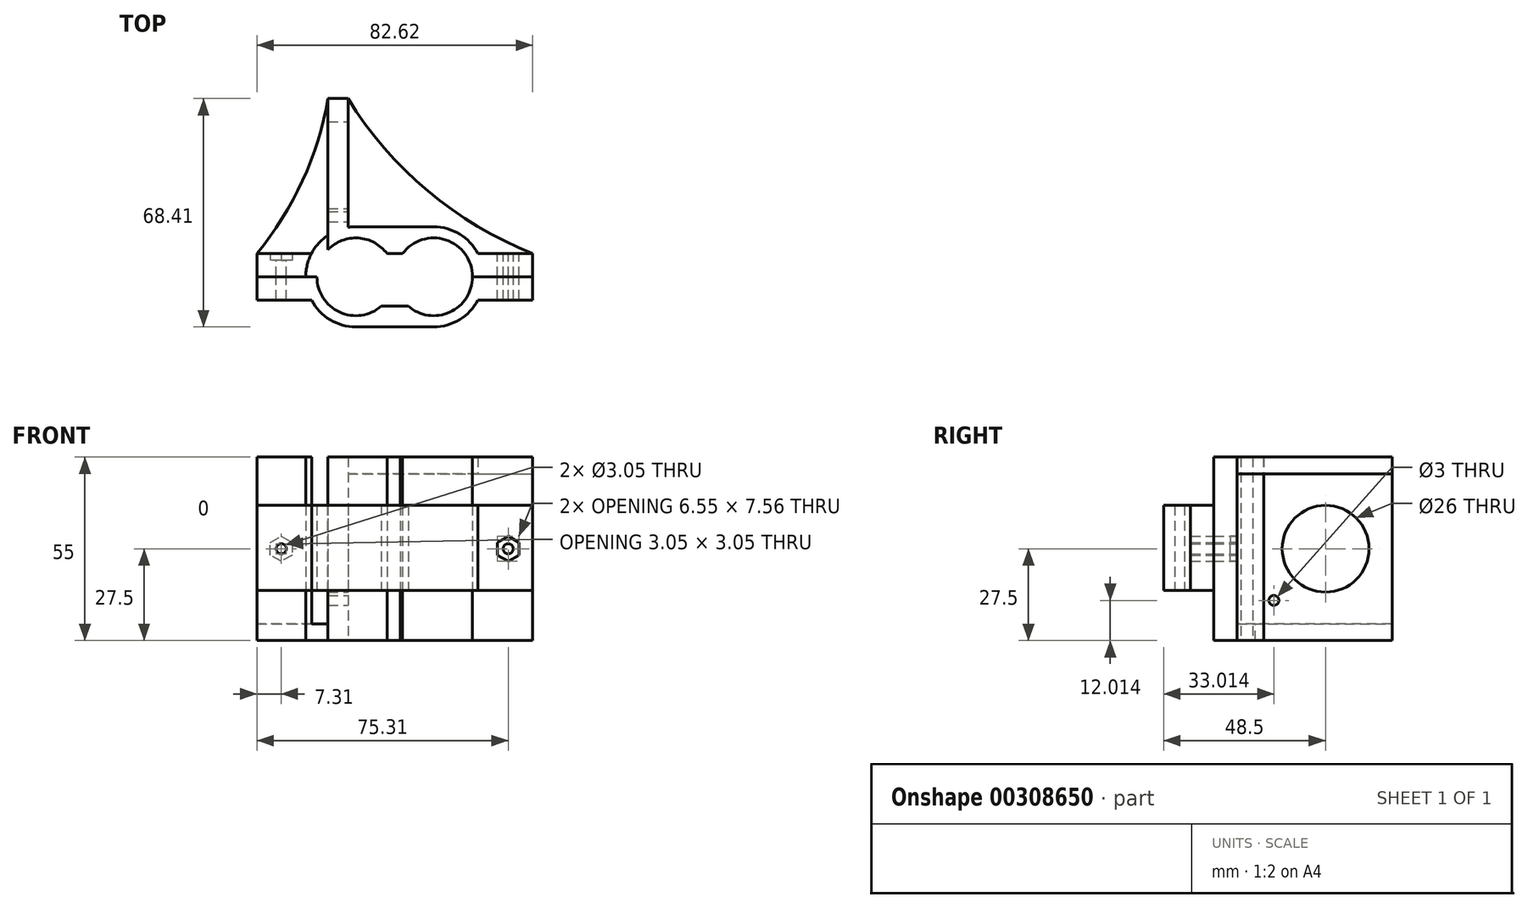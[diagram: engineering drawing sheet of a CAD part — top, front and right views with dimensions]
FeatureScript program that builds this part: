
annotation { "Feature Type Name" : "Feature", "Feature Type Description" : "" }
export const myFeature = defineFeature(function(context is Context, id is Id, definition is map)
    precondition{}
    {
        {
            var Q0;
            Q0=qCreatedBy(makeId("Top.planeOp"),FACE);
            var sketch = newSketch(context, id + "F0", { "sketchPlane" : qUnion([Q0])});
            skArc(sketch, "E0", {"start": v(-2.3, 6.94) * mm, "mid": v(-23.23, 1.27) * mm, "end": v(-4.03, -8.8) * mm});
            skArc(sketch, "E1.MirrorC", {"start": v(2.3, 6.94) * mm, "mid": v(23.23, 1.27) * mm, "end": v(4.03, -8.8) * mm});
            skArc(sketch, "E2", {"start": v(-11.65, 15) * mm, "mid": v(-25.2, -6.45) * mm, "end": v(0, -9.45) * mm});
            skArc(sketch, "E3.MirrorC", {"start": v(11.65, 15) * mm, "mid": v(25.2, -6.45) * mm, "end": v(0, -9.45) * mm});
            skLineSegment(sketch, "E4.0", {"start": v(1.73, 6.93) * mm, "end": v(-2.3, 6.94) * mm});
            skLineSegment(sketch, "E5", {"start": v(-41.3, 7) * mm, "end": v(-41.3, 0) * mm});
            skLineSegment(sketch, "E6", {"start": v(-41.3, 0) * mm, "end": v(-23.3, 0) * mm});
            skLineSegment(sketch, "E7.MirrorCS", {"start": v(1.73, 6.93) * mm, "end": v(2.3, 6.94) * mm});
            skLineSegment(sketch, "E8", {"start": v(-24.92, 7) * mm, "end": v(-41.3, 7) * mm});
            skLineSegment(sketch, "E9", {"start": v(-33.11, 7) * mm, "end": v(-33.11, 0) * mm});
            skLineSegment(sketch, "E10", {"start": v(-4.03, 8.8) * mm, "end": v(4.03, 8.8) * mm});
            skLineSegment(sketch, "E11.MirrorCS", {"start": v(-4.03, -8.8) * mm, "end": v(4.03, -8.8) * mm});
            skLineSegment(sketch, "E12.MirrorCS", {"start": v(-24.92, -7) * mm, "end": v(-41.3, -7) * mm});
            skLineSegment(sketch, "E13.MirrorCS", {"start": v(-41.3, -7) * mm, "end": v(-41.3, 0) * mm});
            skLineSegment(sketch, "E14.MirrorCS", {"start": v(-33.11, -7) * mm, "end": v(-33.11, 0) * mm});
            skLineSegment(sketch, "E15", {"start": v(11.65, -15) * mm, "end": v(-11.65, -15) * mm});
            skLineSegment(sketch, "E16", {"start": v(11.65, 15) * mm, "end": v(-11.65, 15) * mm});
            skLineSegment(sketch, "E17.trimOffspring", {"start": v(-23.3, 0) * mm, "end": v(-26.65, 0) * mm});
            skPoint(sketch, "E18.orphan", {"position": v(0, 0) * mm});
            skLineSegment(sketch, "E19.0", {"start": v(-34.61, 7) * mm, "end": v(-34.61, 0) * mm});
            skLineSegment(sketch, "E20.0", {"start": v(-31.61, 7) * mm, "end": v(-31.61, 0) * mm});
            skLineSegment(sketch, "E21.MirrorCS", {"start": v(-31.61, -7) * mm, "end": v(-31.61, 0) * mm});
            skLineSegment(sketch, "E22.MirrorCS", {"start": v(-34.61, -7) * mm, "end": v(-34.61, 0) * mm});
            skLineSegment(sketch, "E23.MirrorCS", {"start": v(24.92, 7) * mm, "end": v(41.3, 7) * mm});
            skLineSegment(sketch, "E24.MirrorCS", {"start": v(41.3, 0) * mm, "end": v(23.3, 0) * mm});
            skLineSegment(sketch, "E25.MirrorCS", {"start": v(24.92, -7) * mm, "end": v(41.3, -7) * mm});
            skLineSegment(sketch, "E26.MirrorCS", {"start": v(41.3, -7) * mm, "end": v(41.3, 0) * mm});
            skLineSegment(sketch, "E27.MirrorCS", {"start": v(41.3, 7) * mm, "end": v(41.3, 0) * mm});
            skLineSegment(sketch, "E28.MirrorCS", {"start": v(34.61, 7) * mm, "end": v(34.61, 0) * mm});
            skLineSegment(sketch, "E29.MirrorCS", {"start": v(33.11, 7) * mm, "end": v(33.11, 0) * mm});
            skLineSegment(sketch, "E30.MirrorCS", {"start": v(31.61, 7) * mm, "end": v(31.61, 0) * mm});
            skLineSegment(sketch, "E31.MirrorCS", {"start": v(34.61, -7) * mm, "end": v(34.61, 0) * mm});
            skLineSegment(sketch, "E32.MirrorCS", {"start": v(33.11, -7) * mm, "end": v(33.11, 0) * mm});
            skLineSegment(sketch, "E33.MirrorCS", {"start": v(31.61, -7) * mm, "end": v(31.61, 0) * mm});
            skLineSegment(sketch, "E34", {"start": v(-41.3, 0) * mm, "end": v(-47.3, 0) * mm});
            skLineSegment(sketch, "E35", {"start": v(-14, 11.41) * mm, "end": v(-14, 53.41) * mm});
            skLineSegment(sketch, "E36", {"start": v(-14, 53.41) * mm, "end": v(-20, 53.41) * mm});
            skLineSegment(sketch, "E37", {"start": v(-20, 53.41) * mm, "end": v(-20, 8.12) * mm});
            skArc(sketch, "E38", {"start": v(-14, 53.41) * mm, "mid": v(9.9, 25.74) * mm, "end": v(41.3, 7) * mm});
            skArc(sketch, "E39", {"start": v(-41.3, 7) * mm, "mid": v(-27.61, 28.8) * mm, "end": v(-20, 53.41) * mm});
            skSolve(sketch);
        }
        {
            var Q0;
            {var subQ3=sQuery(id+"F0.wireOp",EDGE,"E10");Q0=makeQuery(id+"F0.imprint","IMPRINT",FACE,{"disambiguationData":[TD([[makeQuery(id+"F0.imprint","IMPRINT",EDGE,{"derivedFrom":subQ3}),1.0]])]});}
            var Q1;
            {var subQ5=sQuery(id+"F0.wireOp",EDGE,"E30.MirrorCS");Q1=makeQuery(id+"F0.imprint","IMPRINT",FACE,{"disambiguationData":[TD([[makeQuery(id+"F0.imprint","IMPRINT",EDGE,{"derivedFrom":subQ5}),-1.0]])]});}
            var Q2;
            {var subQ0=sQuery(id+"F0.wireOp",EDGE,"E28.MirrorCS");Q2=makeQuery(id+"F0.imprint","IMPRINT",FACE,{"disambiguationData":[TD([[makeQuery(id+"F0.imprint","IMPRINT",EDGE,{"derivedFrom":subQ0}),-1.0]])]});}
            var Q3;
            {var subQ0=sQuery(id+"F0.wireOp",EDGE,"E29.MirrorCS");Q3=makeQuery(id+"F0.imprint","IMPRINT",FACE,{"disambiguationData":[TD([[makeQuery(id+"F0.imprint","IMPRINT",EDGE,{"derivedFrom":subQ0}),-1.0]])]});}
            var Q4;
            {var subQ0=sQuery(id+"F0.wireOp",EDGE,"E27.MirrorCS");Q4=makeQuery(id+"F0.imprint","IMPRINT",FACE,{"disambiguationData":[TD([[makeQuery(id+"F0.imprint","IMPRINT",EDGE,{"derivedFrom":subQ0}),-1.0]])]});}
            var Q5;
            {var subQ5=sQuery(id+"F0.wireOp",EDGE,"E20.0");Q5=makeQuery(id+"F0.imprint","IMPRINT",FACE,{"disambiguationData":[TD([[makeQuery(id+"F0.imprint","IMPRINT",EDGE,{"derivedFrom":subQ5}),1.0]])]});}
            var Q6;
            {var subQ0=sQuery(id+"F0.wireOp",EDGE,"E9");Q6=makeQuery(id+"F0.imprint","IMPRINT",FACE,{"disambiguationData":[TD([[makeQuery(id+"F0.imprint","IMPRINT",EDGE,{"derivedFrom":subQ0}),1.0]])]});}
            var Q7;
            {var subQ0=sQuery(id+"F0.wireOp",EDGE,"E9");Q7=makeQuery(id+"F0.imprint","IMPRINT",FACE,{"disambiguationData":[TD([[makeQuery(id+"F0.imprint","IMPRINT",EDGE,{"derivedFrom":subQ0}),-1.0]])]});}
            var Q8;
            {var subQ0=sQuery(id+"F0.wireOp",EDGE,"E5");Q8=makeQuery(id+"F0.imprint","IMPRINT",FACE,{"disambiguationData":[TD([[makeQuery(id+"F0.imprint","IMPRINT",EDGE,{"derivedFrom":subQ0}),1.0]])]});}
            var Q9;
            {var subQ1=sQuery(id+"F0.wireOp",EDGE,"E4.0");Q9=makeQuery(id+"F0.imprint","IMPRINT",FACE,{"disambiguationData":[TD([[makeQuery(id+"F0.imprint","IMPRINT",EDGE,{"derivedFrom":subQ1}),-1.0]])]});}
            var Q10;
            {var subQ2=sQuery(id+"F0.wireOp",EDGE,"Vv1cVioz-D9HU-Hz8a-WSvE-FMZzDvxmSNJW");Q10=makeQuery(id+"F0.imprint","IMPRINT",FACE,{"disambiguationData":[TD([[makeQuery(id+"F0.imprint","IMPRINT",EDGE,{"derivedFrom":subQ2}),-1.0]])]});}
            var Q11;
            {var subQ0=sQuery(id+"F0.wireOp",EDGE,"E17.trimOffspring");Q11=makeQuery(id+"F0.imprint","IMPRINT",FACE,{"disambiguationData":[TD([[makeQuery(id+"F0.imprint","IMPRINT",EDGE,{"derivedFrom":subQ0}),-1.0]])]});}
            extrude(context, id + "F1", {"entities" : qUnion([Q0, Q1, Q2, Q3, Q4, Q5, Q6, Q7, Q8, Q9, Q10, Q11]), "depth" : 25 * mm, "hasSecondDirection" : true, "secondDirectionOppositeDirection" : true, "secondDirectionDepth" : 30 * mm});
        }
        {
            var Q0;
            {var subQ0=sQuery(id+"F0.wireOp",EDGE,"E13.MirrorCS");Q0=makeQuery(id+"F0.imprint","IMPRINT",FACE,{"disambiguationData":[TD([[makeQuery(id+"F0.imprint","IMPRINT",EDGE,{"derivedFrom":subQ0}),-1.0]])]});}
            var Q1;
            {var subQ0=sQuery(id+"F0.wireOp",EDGE,"E14.MirrorCS");Q1=makeQuery(id+"F0.imprint","IMPRINT",FACE,{"disambiguationData":[TD([[makeQuery(id+"F0.imprint","IMPRINT",EDGE,{"derivedFrom":subQ0}),1.0]])]});}
            var Q2;
            {var subQ0=sQuery(id+"F0.wireOp",EDGE,"E14.MirrorCS");Q2=makeQuery(id+"F0.imprint","IMPRINT",FACE,{"disambiguationData":[TD([[makeQuery(id+"F0.imprint","IMPRINT",EDGE,{"derivedFrom":subQ0}),-1.0]])]});}
            var Q3;
            {var subQ5=sQuery(id+"F0.wireOp",EDGE,"E21.MirrorCS");Q3=makeQuery(id+"F0.imprint","IMPRINT",FACE,{"disambiguationData":[TD([[makeQuery(id+"F0.imprint","IMPRINT",EDGE,{"derivedFrom":subQ5}),-1.0]])]});}
            var Q4;
            {var subQ0=sQuery(id+"F0.wireOp",EDGE,"E11.MirrorCS");Q4=makeQuery(id+"F0.imprint","IMPRINT",FACE,{"disambiguationData":[TD([[makeQuery(id+"F0.imprint","IMPRINT",EDGE,{"derivedFrom":subQ0}),-1.0]])]});}
            var Q5;
            {var subQ3=sQuery(id+"F0.wireOp",EDGE,"E15");Q5=makeQuery(id+"F0.imprint","IMPRINT",FACE,{"disambiguationData":[TD([[makeQuery(id+"F0.imprint","IMPRINT",EDGE,{"derivedFrom":subQ3}),-1.0]])]});}
            var Q6;
            {var subQ5=sQuery(id+"F0.wireOp",EDGE,"E33.MirrorCS");Q6=makeQuery(id+"F0.imprint","IMPRINT",FACE,{"disambiguationData":[TD([[makeQuery(id+"F0.imprint","IMPRINT",EDGE,{"derivedFrom":subQ5}),1.0]])]});}
            var Q7;
            {var subQ0=sQuery(id+"F0.wireOp",EDGE,"E32.MirrorCS");Q7=makeQuery(id+"F0.imprint","IMPRINT",FACE,{"disambiguationData":[TD([[makeQuery(id+"F0.imprint","IMPRINT",EDGE,{"derivedFrom":subQ0}),1.0]])]});}
            var Q8;
            {var subQ0=sQuery(id+"F0.wireOp",EDGE,"E31.MirrorCS");Q8=makeQuery(id+"F0.imprint","IMPRINT",FACE,{"disambiguationData":[TD([[makeQuery(id+"F0.imprint","IMPRINT",EDGE,{"derivedFrom":subQ0}),1.0]])]});}
            var Q9;
            {var subQ0=sQuery(id+"F0.wireOp",EDGE,"E26.MirrorCS");Q9=makeQuery(id+"F0.imprint","IMPRINT",FACE,{"disambiguationData":[TD([[makeQuery(id+"F0.imprint","IMPRINT",EDGE,{"derivedFrom":subQ0}),1.0]])]});}
            extrude(context, id + "F2", {"entities" : qUnion([Q0, Q1, Q2, Q3, Q4, Q5, Q6, Q7, Q8, Q9]), "depth" : 10.5 * mm, "hasSecondDirection" : true, "secondDirectionOppositeDirection" : true, "secondDirectionDepth" : 15 * mm});
        }
        {
            var Q0;
            Q0=qCreatedBy(makeId("Front.planeOp"),FACE);
            var sketch = newSketch(context, id + "F3", { "sketchPlane" : qUnion([Q0])});
            skCircle(sketch, "E40.cCircle", {"center": v(-34, -2.5) * mm, "radius": 3.28 * mm, "construction": true});
            skLineSegment(sketch, "E40.0", {"start": v(-37.28, -4.4) * mm, "end": v(-37.28, -0.6) * mm});
            skLineSegment(sketch, "E40.1", {"start": v(-37.28, -0.6) * mm, "end": v(-34, 1.28) * mm});
            skLineSegment(sketch, "E40.2", {"start": v(-34, 1.28) * mm, "end": v(-30.72, -0.6) * mm});
            skLineSegment(sketch, "E40.3", {"start": v(-30.72, -0.6) * mm, "end": v(-30.72, -4.4) * mm});
            skLineSegment(sketch, "E40.4", {"start": v(-30.73, -4.4) * mm, "end": v(-34, -6.28) * mm});
            skLineSegment(sketch, "E40.5", {"start": v(-34, -6.28) * mm, "end": v(-37.28, -4.4) * mm});
            skPoint(sketch, "E40.0.midPoint", {"position": v(-37.28, -2.5) * mm});
            skCircle(sketch, "E41", {"center": v(-34, -2.5) * mm, "radius": 1.52 * mm});
            skLineSegment(sketch, "E42.MirrorCS", {"start": v(34, 1.28) * mm, "end": v(30.72, -0.6) * mm});
            skLineSegment(sketch, "E43.MirrorCS", {"start": v(30.72, -4.4) * mm, "end": v(34, -6.28) * mm});
            skLineSegment(sketch, "E44.MirrorCS", {"start": v(34, -6.28) * mm, "end": v(37.28, -4.4) * mm});
            skLineSegment(sketch, "E45.MirrorCS", {"start": v(37.28, -4.4) * mm, "end": v(37.28, -0.6) * mm});
            skLineSegment(sketch, "E46.MirrorCS", {"start": v(30.72, -0.6) * mm, "end": v(30.72, -4.4) * mm});
            skCircle(sketch, "E47.MirrorC", {"center": v(34, -2.5) * mm, "radius": 1.52 * mm});
            skPoint(sketch, "E48.MirrorP", {"position": v(37.28, -2.5) * mm});
            skCircle(sketch, "E49.MirrorC", {"center": v(34, -2.5) * mm, "radius": 3.28 * mm, "construction": true});
            skLineSegment(sketch, "E50.MirrorCS", {"start": v(37.28, -0.6) * mm, "end": v(34, 1.28) * mm});
            skSolve(sketch);
        }
        {
            var Q0;
            Q0=makeQuery(id+"F3.imprint","IMPRINT",FACE,{"disambiguationData":[TD([[makeQuery(id+"F3.imprint","IMPRINT",EDGE,{"derivedFrom":sQuery(id+"F3.wireOp",EDGE,"E47.MirrorC")}),-1.0]])]});
            var Q1;
            Q1=makeQuery(id+"F3.imprint","IMPRINT",FACE,{"disambiguationData":[TD([[makeQuery(id+"F3.imprint","IMPRINT",EDGE,{"derivedFrom":sQuery(id+"F3.wireOp",EDGE,"E41")}),1.0]])]});
            extrude(context, id + "F4", {"entities" : qUnion([Q0, Q1]), "operationType" : NewBodyOperationType.REMOVE, "depth" : 25 * mm, "hasSecondDirection" : true, "secondDirectionOppositeDirection" : true, "secondDirectionDepth" : 25 * mm});
        }
        {
            var Q0;
            Q0=makeQuery(id+"F3.imprint","IMPRINT",FACE,{"disambiguationData":[TD([[makeQuery(id+"F3.imprint","IMPRINT",EDGE,{"derivedFrom":sQuery(id+"F3.wireOp",EDGE,"E42.MirrorCS")}),1.0]])]});
            var Q1;
            Q1=makeQuery(id+"F3.imprint","IMPRINT",FACE,{"disambiguationData":[TD([[makeQuery(id+"F3.imprint","IMPRINT",EDGE,{"derivedFrom":sQuery(id+"F3.wireOp",EDGE,"E40.0")}),-1.0]])]});
            extrude(context, id + "F5", {"entities" : qUnion([Q0, Q1]), "operationType" : NewBodyOperationType.REMOVE, "oppositeDirection" : true, "depth" : 25 * mm, "hasSecondDirection" : true, "secondDirectionOppositeDirection" : true, "secondDirectionDepth" : 5 * mm});
        }
        {
            var Q0;
            Q0=qCreatedBy(makeId("Right.planeOp"),FACE);
            var sketch = newSketch(context, id + "F6", { "sketchPlane" : qUnion([Q0])});
            skCircle(sketch, "E51", {"center": v(33.5, -2.5) * mm, "radius": 13 * mm});
            skLineSegment(sketch, "E52", {"start": v(33.5, -2.5) * mm, "end": v(73.5, -2.5) * mm});
            skLineSegment(sketch, "E53", {"start": v(33.5, -2.5) * mm, "end": v(61.78, 25.78) * mm});
            skCircle(sketch, "E54", {"center": v(48.99, 12.99) * mm, "radius": 1.5 * mm});
            skLineSegment(sketch, "E55", {"start": v(33.5, -2.5) * mm, "end": v(33.5, 7.5) * mm});
            skCircle(sketch, "E56.MirrorC", {"center": v(48.99, -17.99) * mm, "radius": 1.5 * mm});
            skCircle(sketch, "E57.MirrorC", {"center": v(18.01, 12.99) * mm, "radius": 1.5 * mm});
            skCircle(sketch, "E58.MirrorC", {"center": v(18.01, -17.99) * mm, "radius": 1.5 * mm});
            skSolve(sketch);
        }
        {
            var Q0;
            Q0=makeQuery(id+"F0.imprint","IMPRINT",FACE,{"disambiguationData":[TD([[makeQuery(id+"F0.imprint","IMPRINT",EDGE,{"derivedFrom":sQuery(id+"F0.wireOp",EDGE,"E5")}),-1.0]])]});
            var Q1;
            {var subQ0=sQuery(id+"F0.wireOp",EDGE,"HdxULpwj-fMgD-GCkn-AVkN-2g73bKeQRSIG");Q1=makeQuery(id+"F0.imprint","IMPRINT",FACE,{"disambiguationData":[TD([[makeQuery(id+"F0.imprint","IMPRINT",EDGE,{"derivedFrom":subQ0}),1.0]])]});}
            var Q2;
            {var subQ1=sQuery(id+"F0.wireOp",EDGE,"E35");Q2=makeQuery(id+"F0.imprint","IMPRINT",FACE,{"disambiguationData":[TD([[makeQuery(id+"F0.imprint","IMPRINT",EDGE,{"derivedFrom":subQ1}),1.0]])]});}
            var Q3;
            {var subQ0=sQuery(id+"F0.wireOp",EDGE,"yx3PEQPX-n8Hq-1DG4-7nrZ-ExZ4iS4Ewtql");Q3=makeQuery(id+"F0.imprint","IMPRINT",FACE,{"disambiguationData":[TD([[makeQuery(id+"F0.imprint","IMPRINT",EDGE,{"derivedFrom":subQ0}),1.0]])]});}
            extrude(context, id + "F7", {"entities" : qUnion([Q0, Q1, Q2, Q3]), "operationType" : NewBodyOperationType.ADD, "depth" : 25 * mm, "hasSecondDirection" : true, "secondDirectionOppositeDirection" : true, "secondDirectionDepth" : 30 * mm});
        }
        {
            var Q0;
            {var subQ0=sQuery(id+"F6.wireOp",EDGE,"E52");var subQ1=sQuery(id+"F6.wireOp",EDGE,"E51");var subQ2=makeQuery(id+"F6.imprint","INTERSECT",VERTEX,{"derivedFrom":[subQ1,subQ0]});Q0=makeQuery(id+"F6.imprint","IMPRINT",FACE,{"disambiguationData":[TD([[makeQuery(id+"F6.imprint","IMPRINT",EDGE,{"disambiguationData":[TD([[subQ2,1.0]])],"derivedFrom":subQ1}),1.0]])]});}
            var Q1;
            {var subQ0=sQuery(id+"F6.wireOp",EDGE,"E52");var subQ1=sQuery(id+"F6.wireOp",EDGE,"E51");var subQ2=makeQuery(id+"F6.imprint","INTERSECT",VERTEX,{"derivedFrom":[subQ1,subQ0]});Q1=makeQuery(id+"F6.imprint","IMPRINT",FACE,{"disambiguationData":[TD([[makeQuery(id+"F6.imprint","IMPRINT",EDGE,{"disambiguationData":[TD([[subQ2,-1.0]])],"derivedFrom":subQ1}),1.0]])]});}
            var Q2;
            {var subQ0=sQuery(id+"F6.wireOp",EDGE,"E54");var subQ1=sQuery(id+"F6.wireOp",EDGE,"E53");var subQ2=makeQuery(id+"F6.imprint","INTERSECT",VERTEX,{"disambiguationData":[OD(0.0)],"derivedFrom":[subQ1,subQ0]});Q2=makeQuery(id+"F6.imprint","IMPRINT",FACE,{"disambiguationData":[TD([[makeQuery(id+"F6.imprint","IMPRINT",EDGE,{"disambiguationData":[TD([[subQ2,-1.0]])],"derivedFrom":subQ1}),1.0]])]});}
            var Q3;
            {var subQ0=sQuery(id+"F6.wireOp",EDGE,"E54");var subQ1=sQuery(id+"F6.wireOp",EDGE,"E53");var subQ2=makeQuery(id+"F6.imprint","INTERSECT",VERTEX,{"disambiguationData":[OD(0.0)],"derivedFrom":[subQ1,subQ0]});Q3=makeQuery(id+"F6.imprint","IMPRINT",FACE,{"disambiguationData":[TD([[makeQuery(id+"F6.imprint","IMPRINT",EDGE,{"disambiguationData":[TD([[subQ2,-1.0]])],"derivedFrom":subQ1}),-1.0]])]});}
            var Q4;
            Q4=makeQuery(id+"F6.imprint","IMPRINT",FACE,{"disambiguationData":[TD([[makeQuery(id+"F6.imprint","IMPRINT",EDGE,{"derivedFrom":sQuery(id+"F6.wireOp",EDGE,"E57.MirrorC")}),-1.0]])]});
            var Q5;
            Q5=makeQuery(id+"F6.imprint","IMPRINT",FACE,{"disambiguationData":[TD([[makeQuery(id+"F6.imprint","IMPRINT",EDGE,{"derivedFrom":sQuery(id+"F6.wireOp",EDGE,"E56.MirrorC")}),-1.0]])]});
            var Q6;
            Q6=makeQuery(id+"F6.imprint","IMPRINT",FACE,{"disambiguationData":[TD([[makeQuery(id+"F6.imprint","IMPRINT",EDGE,{"derivedFrom":sQuery(id+"F6.wireOp",EDGE,"E58.MirrorC")}),1.0]])]});
            var Q7;
            {var subQ0=sQuery(id+"F6.wireOp",EDGE,"kWAtsnuM-qsjY-J9rG-5AT4-uiAB8qKF9Tyo");var subQ1=sQuery(id+"F6.wireOp",EDGE,"E53");var subQ2=makeQuery(id+"F6.imprint","INTERSECT",VERTEX,{"disambiguationData":[OD(0.0)],"derivedFrom":[subQ1,subQ0]});Q7=makeQuery(id+"F6.imprint","IMPRINT",FACE,{"disambiguationData":[TD([[makeQuery(id+"F6.imprint","IMPRINT",EDGE,{"disambiguationData":[TD([[subQ2,-1.0]])],"derivedFrom":subQ1}),-1.0]])]});}
            var Q8;
            {var subQ0=sQuery(id+"F6.wireOp",EDGE,"kWAtsnuM-qsjY-J9rG-5AT4-uiAB8qKF9Tyo");var subQ1=sQuery(id+"F6.wireOp",EDGE,"E53");var subQ2=makeQuery(id+"F6.imprint","INTERSECT",VERTEX,{"disambiguationData":[OD(0.0)],"derivedFrom":[subQ1,subQ0]});Q8=makeQuery(id+"F6.imprint","IMPRINT",FACE,{"disambiguationData":[TD([[makeQuery(id+"F6.imprint","IMPRINT",EDGE,{"disambiguationData":[TD([[subQ2,-1.0]])],"derivedFrom":subQ1}),1.0]])]});}
            extrude(context, id + "F8", {"entities" : qUnion([Q0, Q1, Q2, Q3, Q4, Q5, Q6, Q7, Q8]), "operationType" : NewBodyOperationType.REMOVE, "oppositeDirection" : true, "depth" : 50 * mm});
        }
        {
            var Q0;
            {var subQ0=sQuery(id+"F0.wireOp",EDGE,"hm5gfie0-yzco-bGOd-GiOx-wxARVuob9ml5");Q0=makeQuery(id+"F0.imprint","IMPRINT",FACE,{"disambiguationData":[TD([[makeQuery(id+"F0.imprint","IMPRINT",EDGE,{"derivedFrom":subQ0}),-1.0]])]});}
            var Q1;
            {var subQ8=sQuery(id+"F0.wireOp",EDGE,"E16");Q1=makeQuery(id+"F0.imprint","IMPRINT",FACE,{"disambiguationData":[TD([[makeQuery(id+"F0.imprint","IMPRINT",EDGE,{"derivedFrom":subQ8}),-1.0]])]});}
            extrude(context, id + "F9", {"entities" : qUnion([Q0, Q1]), "depth" : 25 * mm, "hasSecondDirection" : true, "secondDirectionOppositeDirection" : false, "secondDirectionDepth" : 20 * mm});
        }
        {
            var Q0;
            {var subQ6=sQuery(id+"F0.wireOp",EDGE,"E39");Q0=makeQuery(id+"F0.imprint","IMPRINT",FACE,{"disambiguationData":[TD([[makeQuery(id+"F0.imprint","IMPRINT",EDGE,{"derivedFrom":subQ6}),-1.0]])]});}
            extrude(context, id + "F10", {"entities" : qUnion([Q0]), "operationType" : NewBodyOperationType.ADD, "oppositeDirection" : true, "depth" : 30 * mm, "hasSecondDirection" : true, "secondDirectionOppositeDirection" : true, "secondDirectionDepth" : 25 * mm});
        }
    });
